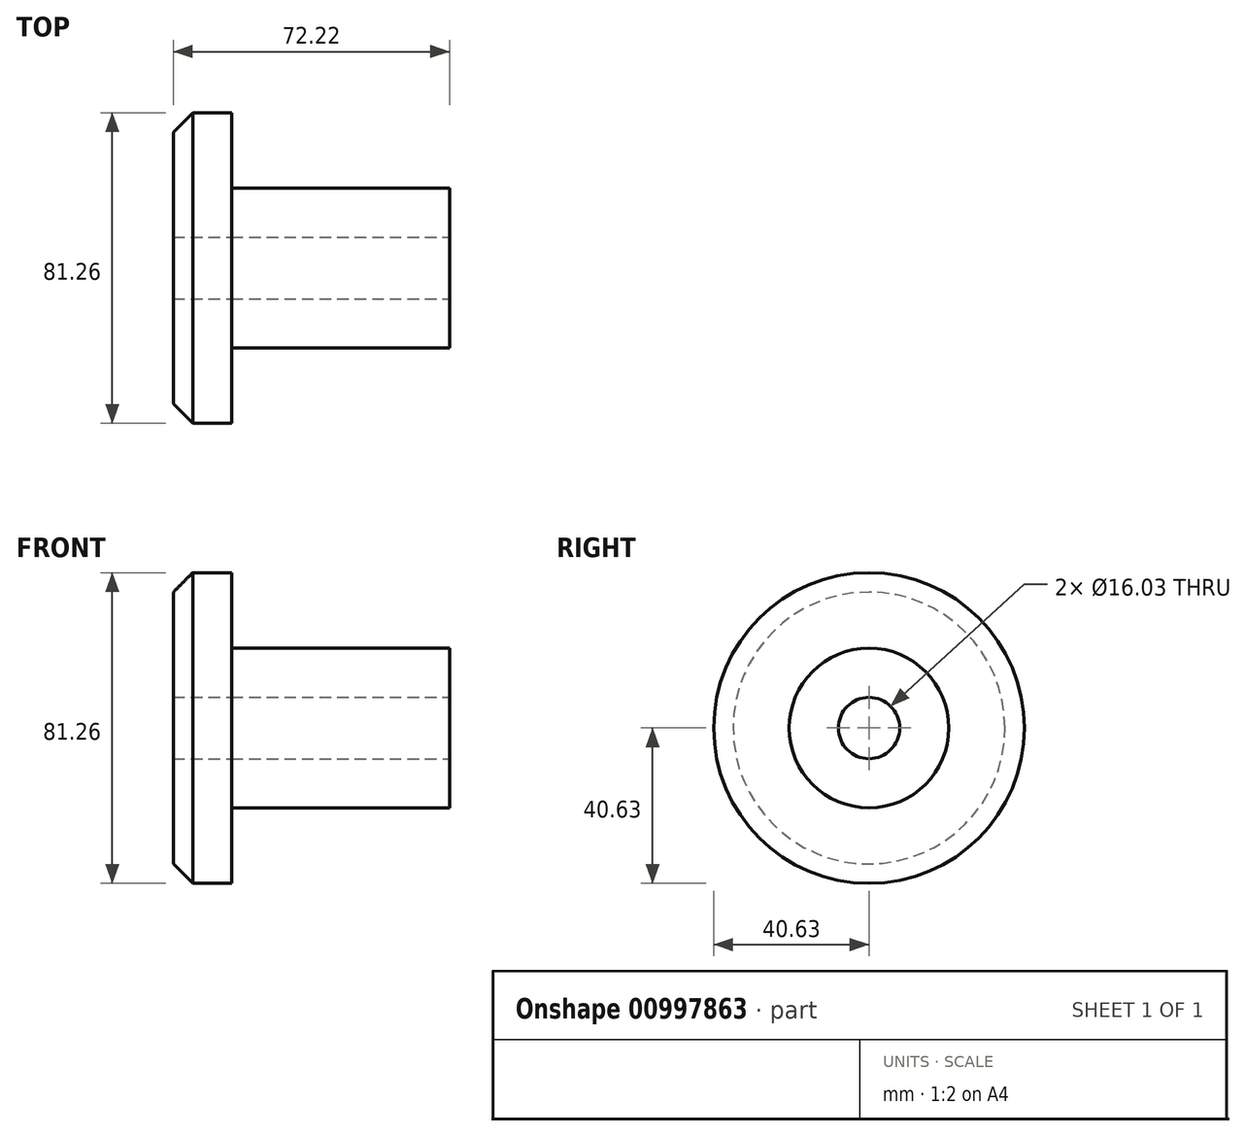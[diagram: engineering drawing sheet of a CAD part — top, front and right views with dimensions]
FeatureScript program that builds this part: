
annotation { "Feature Type Name" : "Feature", "Feature Type Description" : "" }
export const myFeature = defineFeature(function(context is Context, id is Id, definition is map)
    precondition{}
    {
        {
            var Q0;
            Q0=qCreatedBy(makeId("Front.planeOp"),FACE);
            var sketch = newSketch(context, id + "F0", { "sketchPlane" : qUnion([Q0])});
            skLineSegment(sketch, "E0.bottom", {"start": v(0, 0) * mm, "end": v(56.99, 0) * mm});
            skLineSegment(sketch, "E0.top", {"start": v(0, 20.88) * mm, "end": v(56.99, 20.88) * mm});
            skLineSegment(sketch, "E0.left", {"start": v(0, 0) * mm, "end": v(0, 20.88) * mm});
            skLineSegment(sketch, "E0.right", {"start": v(56.99, 0) * mm, "end": v(56.99, 20.88) * mm});
            skSolve(sketch);
        }
        {
            var Q0;
            Q0=qCreatedBy(makeId("Front.planeOp"),FACE);
            var sketch = newSketch(context, id + "F1", { "sketchPlane" : qUnion([Q0])});
            skLineSegment(sketch, "E1.bottom", {"start": v(0, 0) * mm, "end": v(-15.23, 0) * mm});
            skLineSegment(sketch, "E1.top", {"start": v(0, 40.63) * mm, "end": v(-15.23, 40.63) * mm});
            skLineSegment(sketch, "E1.left", {"start": v(0, 0) * mm, "end": v(0, 40.63) * mm});
            skLineSegment(sketch, "E1.right", {"start": v(-15.23, 0) * mm, "end": v(-15.23, 40.63) * mm});
            skSolve(sketch);
        }
        {
            var Q0;
            Q0=qCreatedBy(makeId("Front.planeOp"),FACE);
            var sketch = newSketch(context, id + "F2", { "sketchPlane" : qUnion([Q0])});
            skLineSegment(sketch, "E2", {"start": v(-49.09, 0) * mm, "end": v(71.1, 0) * mm, "construction": true});
            skSolve(sketch);
        }
        {
            var Q0;
            Q0=makeQuery(id+"F0.imprint","IMPRINT",FACE,{"disambiguationData":[TD([[makeQuery(id+"F0.imprint","IMPRINT",EDGE,{"derivedFrom":sQuery(id+"F0.wireOp",EDGE,"E0.bottom")}),1.0]])]});
            var Q1;
            Q1=makeQuery(id+"F1.imprint","IMPRINT",FACE,{"disambiguationData":[TD([[makeQuery(id+"F1.imprint","IMPRINT",EDGE,{"derivedFrom":sQuery(id+"F1.wireOp",EDGE,"E1.bottom")}),-1.0]])]});
            var Q2;
            Q2=sQuery(id+"F2.wireOp",EDGE,"E2");
            revolve(context, id + "F3", {"surfaceOperationType" : NewSurfaceOperationType.NEW, "entities" : qUnion([Q0, Q1]), "axis" : qUnion([Q2]), "revolveType" : RevolveType.FULL});
        }
        {
            var Q0;
            Q0=makeQuery(id+"F3.opRevolve","SWEPT_FACE",FACE,{"disambiguationData":[OSD([sQuery(id+"F0.wireOp",EDGE,"E0.right")])]});
            var sketch = newSketch(context, id + "F4", { "sketchPlane" : qUnion([Q0])});
            skCircle(sketch, "E3", {"center": v(0, 0) * mm, "radius": 8.01 * mm});
            skSolve(sketch);
        }
        {
            var Q0;
            Q0=makeQuery(id+"F4.imprint","IMPRINT",FACE,{"disambiguationData":[TD([[makeQuery(id+"F4.imprint","IMPRINT",EDGE,{"derivedFrom":sQuery(id+"F4.wireOp",EDGE,"E3")}),1.0]])]});
            extrude(context, id + "F5", {"entities" : qUnion([Q0]), "operationType" : NewBodyOperationType.REMOVE, "endBound" : BoundingType.THROUGH_ALL, "oppositeDirection" : true, "depth" : 27.7 * mm, "offsetDistance" : 25.4 * mm});
        }
        {
            var Q0;
            Q0=makeQuery(id+"F3.opRevolve","SWEPT_EDGE",EDGE,{"disambiguationData":[OSD([sQuery(id+"F1.wireOp",EDGE,"E1.top"),sQuery(id+"F1.wireOp",EDGE,"E1.right")])]});
            chamfer(context, id + "F6", {"entities" : qUnion([Q0]), "width" : 5.08 * mm, "tangentPropagation" : true});
        }
    });
